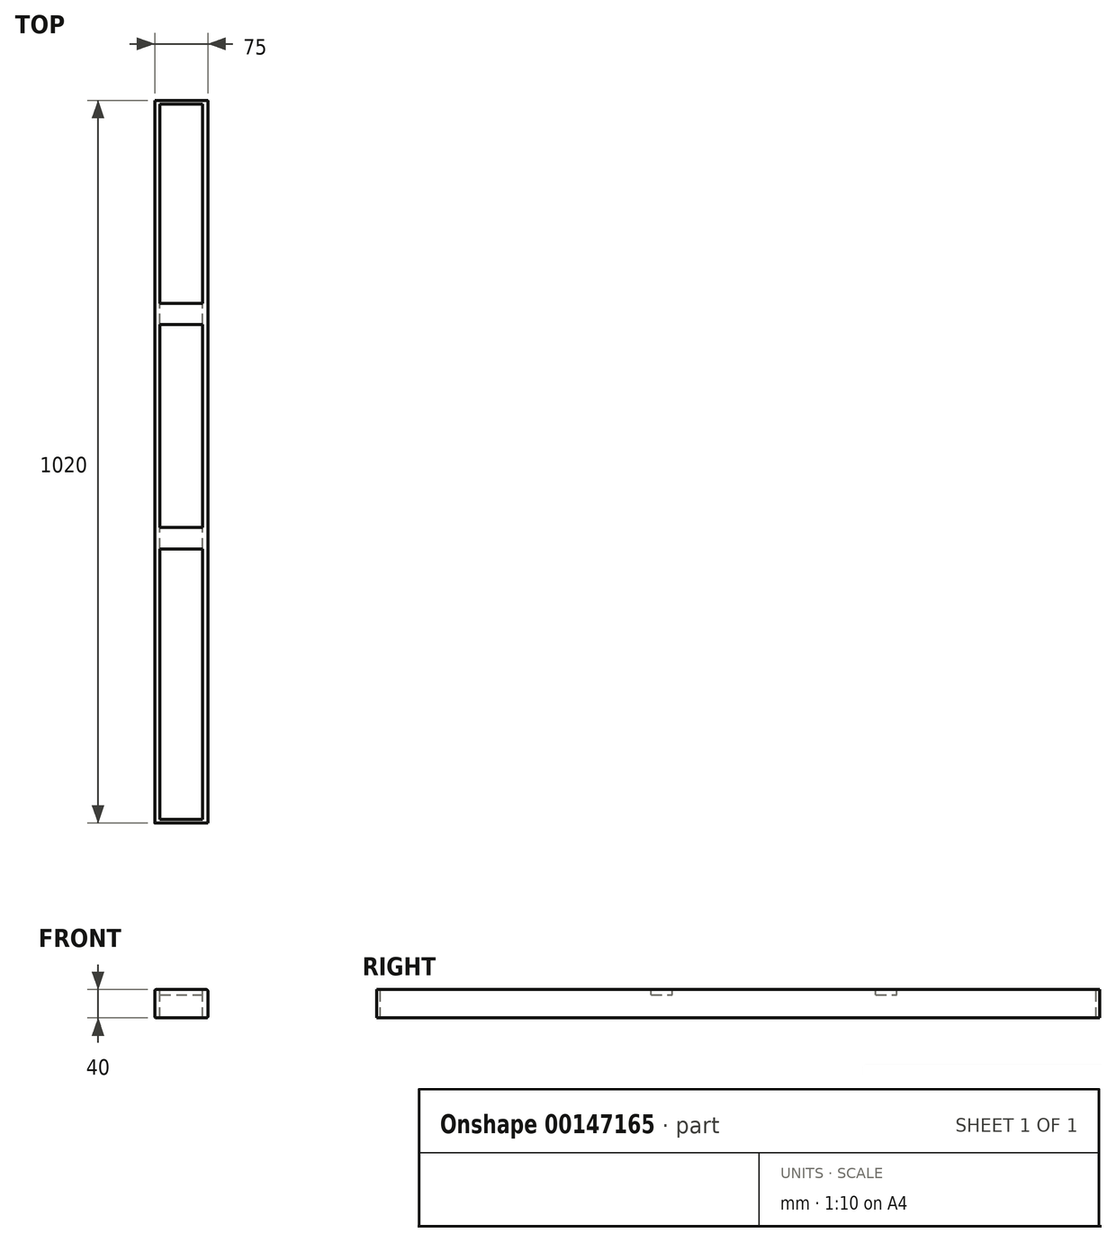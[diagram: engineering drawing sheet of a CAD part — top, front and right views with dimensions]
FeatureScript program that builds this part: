
annotation { "Feature Type Name" : "Feature", "Feature Type Description" : "" }
export const myFeature = defineFeature(function(context is Context, id is Id, definition is map)
    precondition{}
    {
        {
            var Q0;
            Q0=qCreatedBy(makeId("Front.planeOp"),FACE);
            var sketch = newSketch(context, id + "F0", { "sketchPlane" : qUnion([Q0])});
            skLineSegment(sketch, "E0.bottom", {"start": v(37.5, -20) * mm, "end": v(30, -20) * mm});
            skLineSegment(sketch, "E0.top", {"start": v(37.5, 20) * mm, "end": v(-37.5, 20) * mm});
            skLineSegment(sketch, "E0.left", {"start": v(37.5, -20) * mm, "end": v(37.5, 20) * mm});
            skLineSegment(sketch, "E0.right", {"start": v(-37.5, -20) * mm, "end": v(-37.5, 20) * mm});
            skPoint(sketch, "E0.middle", {"position": v(0, 0) * mm});
            skLineSegment(sketch, "E1.top", {"start": v(30, 12.5) * mm, "end": v(-30, 12.5) * mm});
            skLineSegment(sketch, "E1.left", {"start": v(30, -12.5) * mm, "end": v(30, 12.5) * mm});
            skLineSegment(sketch, "E1.right", {"start": v(-30, -12.5) * mm, "end": v(-30, 12.5) * mm});
            skLineSegment(sketch, "E2", {"start": v(-30, -12.5) * mm, "end": v(-30, -20) * mm});
            skLineSegment(sketch, "E3", {"start": v(30, -12.5) * mm, "end": v(30, -20) * mm});
            skLineSegment(sketch, "E4.trimOffspring", {"start": v(-30, -20) * mm, "end": v(-37.5, -20) * mm});
            skSolve(sketch);
        }
        {
            var Q0;
            Q0=makeQuery(id+"F0.imprint","IMPRINT",FACE,{"disambiguationData":[TD([[makeQuery(id+"F0.imprint","IMPRINT",EDGE,{"derivedFrom":sQuery(id+"F0.wireOp",EDGE,"E0.bottom")}),-1.0]])]});
            extrude(context, id + "F1", {"entities" : qUnion([Q0]), "depth" : 1020 * mm});
        }
        {
            var Q0;
            Q0=makeQuery(id+"F1.opExtrude","SWEPT_FACE",FACE,{"disambiguationData":[OSD([sQuery(id+"F0.wireOp",EDGE,"E0.top")])]});
            var sketch = newSketch(context, id + "F2", { "sketchPlane" : qUnion([Q0])});
            skLineSegment(sketch, "E5.bottom", {"start": v(30, -1015) * mm, "end": v(-30, -1015) * mm});
            skLineSegment(sketch, "E5.top", {"start": v(30, -632.88) * mm, "end": v(-30, -632.88) * mm});
            skLineSegment(sketch, "E5.left", {"start": v(30, -1015) * mm, "end": v(30, -632.88) * mm});
            skLineSegment(sketch, "E5.right", {"start": v(-30, -1015) * mm, "end": v(-30, -632.88) * mm});
            skPoint(sketch, "E5.middle", {"position": v(0, -510) * mm});
            skPoint(sketch, "E5.middle.positionSnap0", {"position": v(-37.5, -510) * mm});
            skPoint(sketch, "E5.centerSnap0", {"position": v(-37.5, -510) * mm});
            skLineSegment(sketch, "E6.bottom", {"start": v(30, -602.88) * mm, "end": v(-30, -602.88) * mm});
            skLineSegment(sketch, "E6.top", {"start": v(30, -316.09) * mm, "end": v(-30, -316.09) * mm});
            skLineSegment(sketch, "E6.left", {"start": v(30, -602.88) * mm, "end": v(30, -316.09) * mm});
            skLineSegment(sketch, "E6.right", {"start": v(-30, -602.88) * mm, "end": v(-30, -316.09) * mm});
            skLineSegment(sketch, "E7.bottom", {"start": v(30, -286.09) * mm, "end": v(-30, -286.09) * mm});
            skLineSegment(sketch, "E7.top", {"start": v(30, -5) * mm, "end": v(-30, -5) * mm});
            skLineSegment(sketch, "E7.left", {"start": v(30, -286.09) * mm, "end": v(30, -5) * mm});
            skLineSegment(sketch, "E7.right", {"start": v(-30, -286.09) * mm, "end": v(-30, -5) * mm});
            skSolve(sketch);
        }
        {
            var Q0;
            Q0=qSketchRegion(id+"F2",true);
            extrude(context, id + "F3", {"entities" : qUnion([Q0]), "operationType" : NewBodyOperationType.REMOVE, "oppositeDirection" : true, "depth" : 60 * mm});
        }
        {
            var Q0;
            {var subQ4=sQuery(id+"F0.wireOp",EDGE,"E1.top");Q0=makeQuery(id+"F3.boolean.opBoolean","SPLIT",FACE,{"disambiguationData":[TD([makeQuery(id+"F3.opExtrude","SWEPT_FACE",FACE,{"disambiguationData":[OSD([sQuery(id+"F2.wireOp",EDGE,"E5.bottom")])]})])],"derivedFrom":makeQuery(id+"F1.opExtrude","SWEPT_FACE",FACE,{"disambiguationData":[OSD([subQ4])]})});}
            var Q1;
            {var subQ4=sQuery(id+"F0.wireOp",EDGE,"E1.top");Q1=makeQuery(id+"F3.boolean.opBoolean","SPLIT",FACE,{"disambiguationData":[TD([makeQuery(id+"F3.opExtrude","SWEPT_FACE",FACE,{"disambiguationData":[OSD([sQuery(id+"F2.wireOp",EDGE,"E7.top")])]})])],"derivedFrom":makeQuery(id+"F1.opExtrude","SWEPT_FACE",FACE,{"disambiguationData":[OSD([subQ4])]})});}
            extrude(context, id + "F4", {"entities" : qUnion([Q0, Q1]), "operationType" : NewBodyOperationType.ADD, "depth" : 32.5 * mm});
        }
        {
            var Q0;
            Q0=makeQuery(id+"F1.opExtrude","SWEPT_EDGE",EDGE,{"disambiguationData":[OSD([sQuery(id+"F0.wireOp",EDGE,"E0.top"),sQuery(id+"F0.wireOp",EDGE,"E0.right")])]});
            var Q1;
            Q1=makeQuery(id+"F1.opExtrude","SWEPT_EDGE",EDGE,{"disambiguationData":[OSD([sQuery(id+"F0.wireOp",EDGE,"E0.top"),sQuery(id+"F0.wireOp",EDGE,"E0.left")])]});
            var Q2;
            Q2=makeQuery(id+"F1.opExtrude","SWEPT_EDGE",EDGE,{"disambiguationData":[OSD([sQuery(id+"F0.wireOp",EDGE,"E0.right"),sQuery(id+"F0.wireOp",EDGE,"E4.trimOffspring")])]});
            var Q3;
            Q3=makeQuery(id+"F1.opExtrude","SWEPT_EDGE",EDGE,{"disambiguationData":[OSD([sQuery(id+"F0.wireOp",EDGE,"E0.bottom"),sQuery(id+"F0.wireOp",EDGE,"E0.left")])]});
            fillet(context, id + "F5", {"entities" : qUnion([Q0, Q1, Q2, Q3]), "radius" : 2 * mm, "tangentPropagation" : true, "allowEdgeOverflow" : false});
        }
    });
